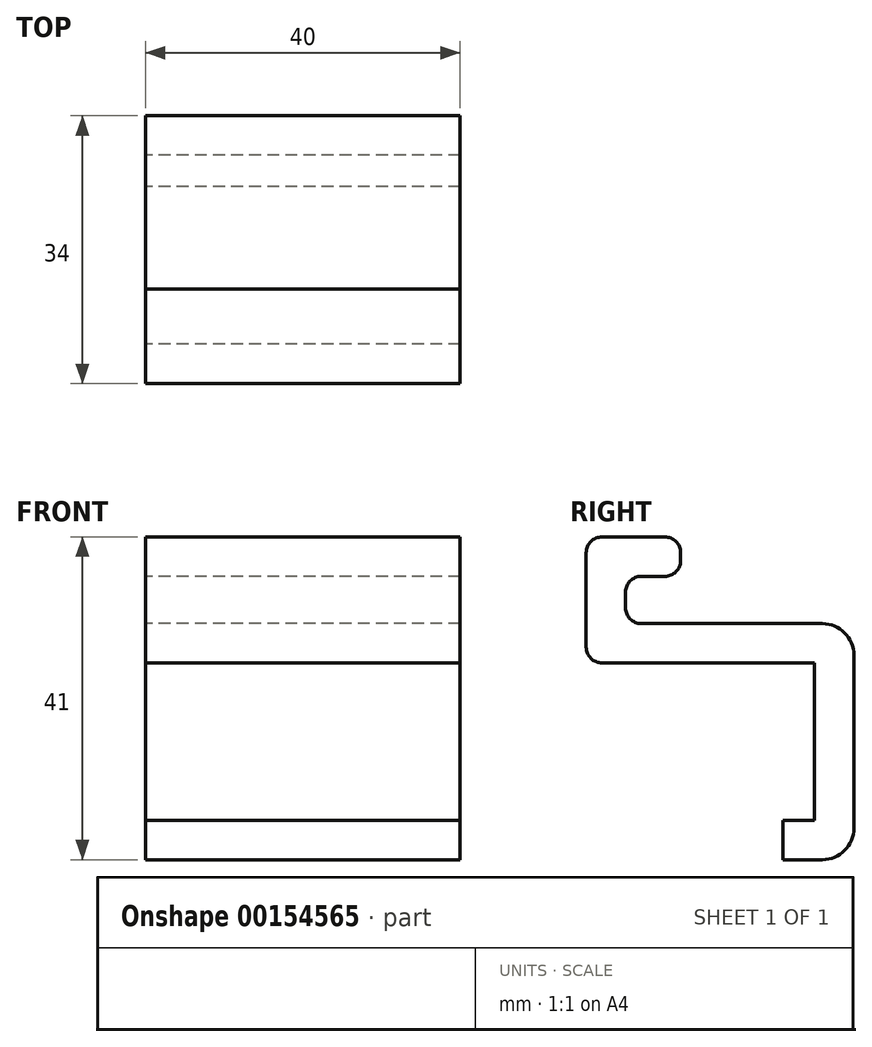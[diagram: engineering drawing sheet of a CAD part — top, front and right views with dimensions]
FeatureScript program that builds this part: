
annotation { "Feature Type Name" : "Feature", "Feature Type Description" : "" }
export const myFeature = defineFeature(function(context is Context, id is Id, definition is map)
    precondition{}
    {
        {
            var Q0;
            Q0=qCreatedBy(makeId("Right.planeOp"),FACE);
            var sketch = newSketch(context, id + "F0", { "sketchPlane" : qUnion([Q0])});
            skLineSegment(sketch, "E0", {"start": v(-13.8, -28.5) * mm, "end": v(-9.8, -28.5) * mm});
            skLineSegment(sketch, "E1", {"start": v(-9.8, -28.5) * mm, "end": v(-9.8, -8.5) * mm});
            skLineSegment(sketch, "E2", {"start": v(-9.8, -8.5) * mm, "end": v(-38.8, -8.5) * mm});
            skLineSegment(sketch, "E3", {"start": v(-33.8, -3.5) * mm, "end": v(-4.8, -3.5) * mm});
            skLineSegment(sketch, "E4", {"start": v(-4.8, -3.5) * mm, "end": v(-4.8, -33.5) * mm});
            skLineSegment(sketch, "E5", {"start": v(-4.8, -33.5) * mm, "end": v(-13.8, -33.5) * mm});
            skLineSegment(sketch, "E6", {"start": v(-13.8, -33.5) * mm, "end": v(-13.8, -28.5) * mm});
            skLineSegment(sketch, "E7", {"start": v(-33.8, -3.5) * mm, "end": v(-33.8, 2.5) * mm});
            skLineSegment(sketch, "E8", {"start": v(-33.8, 2.5) * mm, "end": v(-26.8, 2.5) * mm});
            skLineSegment(sketch, "E9", {"start": v(-26.8, 2.5) * mm, "end": v(-26.8, 7.5) * mm});
            skLineSegment(sketch, "E10", {"start": v(-26.8, 7.5) * mm, "end": v(-38.8, 7.5) * mm});
            skLineSegment(sketch, "E11", {"start": v(-38.8, 7.5) * mm, "end": v(-38.8, -8.5) * mm});
            skSolve(sketch);
        }
        {
            var Q0;
            Q0 = qSketchRegion(id + "F0", true);
            extrude(context, id + "F1", {"entities" : qUnion([Q0]), "endBound" : BoundingType.SYMMETRIC, "depth" : 40 * mm});
        }
        {
            var Q0;
            Q0=makeQuery(id+"F1.opExtrude","SWEPT_EDGE",EDGE,{"disambiguationData":[OSD([sQuery(id+"F0.wireOp",EDGE,"E3"),sQuery(id+"F0.wireOp",EDGE,"E4")])]});
            fillet(context, id + "F2", {"entities" : qUnion([Q0]), "radius" : 4 * mm, "tangentPropagation" : true, "allowEdgeOverflow" : false});
        }
        {
            var Q0;
            Q0=makeQuery(id+"F1.opExtrude","SWEPT_EDGE",EDGE,{"disambiguationData":[OSD([sQuery(id+"F0.wireOp",EDGE,"E4"),sQuery(id+"F0.wireOp",EDGE,"E5")])]});
            fillet(context, id + "F3", {"entities" : qUnion([Q0]), "radius" : 4 * mm, "tangentPropagation" : true, "allowEdgeOverflow" : false});
        }
        {
            var Q0;
            Q0=makeQuery(id+"F1.opExtrude","SWEPT_EDGE",EDGE,{"disambiguationData":[OSD([sQuery(id+"F0.wireOp",EDGE,"E7"),sQuery(id+"F0.wireOp",EDGE,"E8")])]});
            var Q1;
            Q1=makeQuery(id+"F1.opExtrude","SWEPT_EDGE",EDGE,{"disambiguationData":[OSD([sQuery(id+"F0.wireOp",EDGE,"E8"),sQuery(id+"F0.wireOp",EDGE,"E9")])]});
            var Q2;
            Q2=makeQuery(id+"F1.opExtrude","SWEPT_EDGE",EDGE,{"disambiguationData":[OSD([sQuery(id+"F0.wireOp",EDGE,"E9"),sQuery(id+"F0.wireOp",EDGE,"E10")])]});
            var Q3;
            Q3=makeQuery(id+"F1.opExtrude","SWEPT_EDGE",EDGE,{"disambiguationData":[OSD([sQuery(id+"F0.wireOp",EDGE,"E10"),sQuery(id+"F0.wireOp",EDGE,"E11")])]});
            var Q4;
            Q4=makeQuery(id+"F1.opExtrude","SWEPT_EDGE",EDGE,{"disambiguationData":[OSD([sQuery(id+"F0.wireOp",EDGE,"E2"),sQuery(id+"F0.wireOp",EDGE,"E11")])]});
            var Q5;
            Q5=makeQuery(id+"F1.opExtrude","SWEPT_EDGE",EDGE,{"disambiguationData":[OSD([sQuery(id+"F0.wireOp",EDGE,"E3"),sQuery(id+"F0.wireOp",EDGE,"E7")])]});
            fillet(context, id + "F4", {"entities" : qUnion([Q0, Q1, Q2, Q3, Q4, Q5]), "radius" : 2 * mm, "tangentPropagation" : true, "allowEdgeOverflow" : false});
        }
    });
